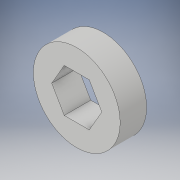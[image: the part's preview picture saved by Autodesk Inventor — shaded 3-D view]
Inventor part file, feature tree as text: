
AUTODESK INVENTOR PART (.ipt)
format: ipt  version: 2018 (Build 220112000, 112)  size: 102,912 bytes
history: native  units: in
note: dims shown in document units (in); Inventor stores cm internally (conversion verified against a paired STEP export)
features: extrude x1, sketch x1
ambient origin geometry x8: Origin, YZ Plane, XZ Plane, XY Plane, X Axis, Y Axis, Z Axis, Center Point
bodies: Solid1 (feature_tree)
feature tree (2):
  extrude  "Extrusion1"  Depth=0.5in
  sketch  "Sketch1"  dims[d0=1.0in d1=0.5in d2=0.305in d3=0.0in]
